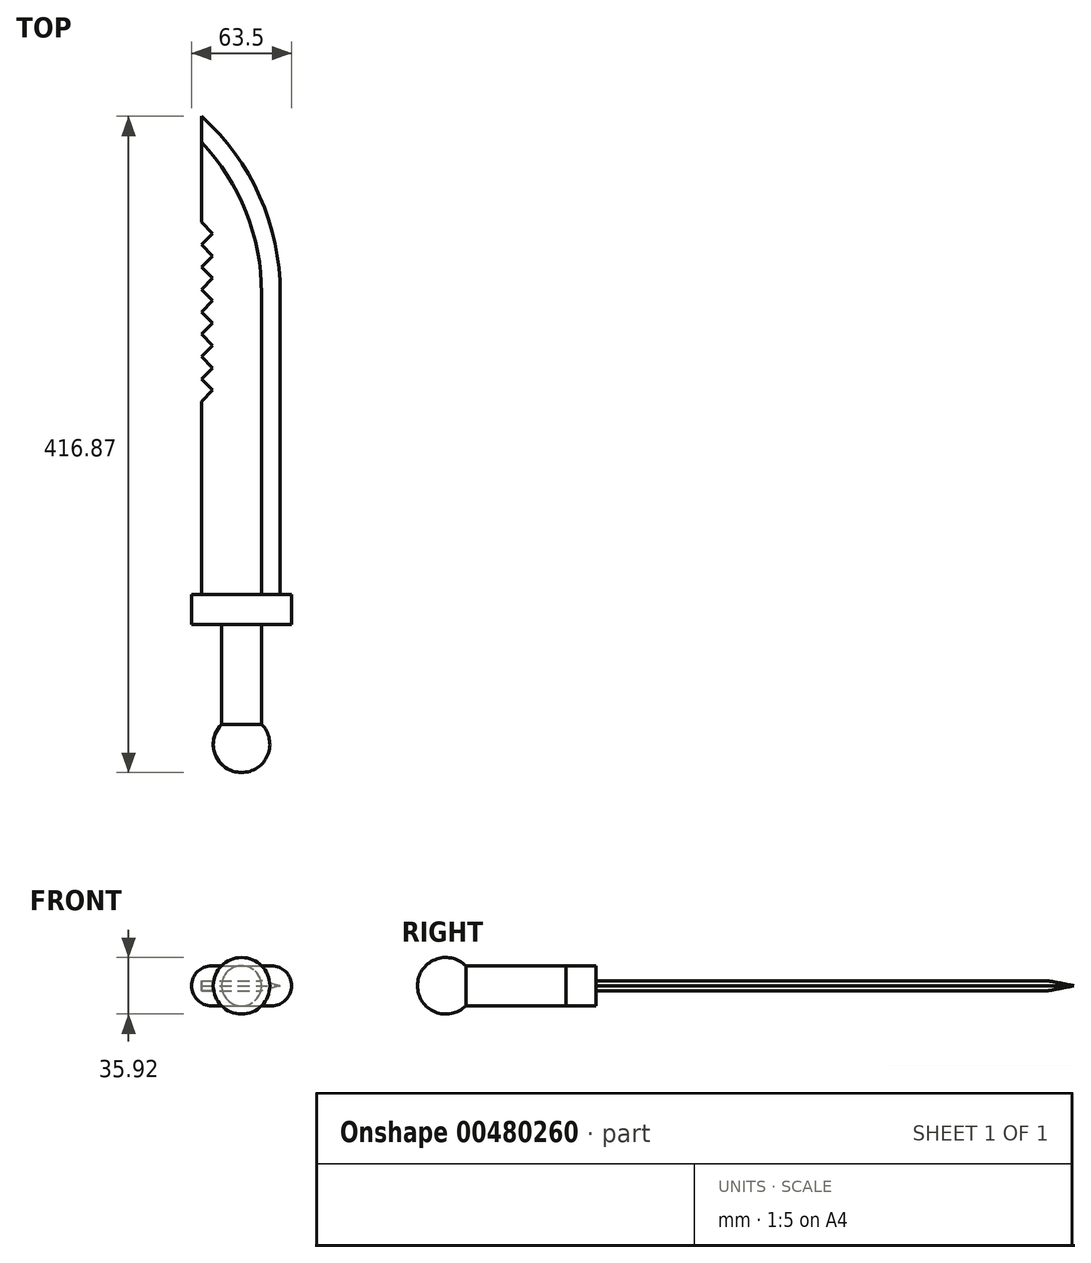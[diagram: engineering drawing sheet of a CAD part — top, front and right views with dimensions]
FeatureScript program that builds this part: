
annotation { "Feature Type Name" : "Feature", "Feature Type Description" : "" }
export const myFeature = defineFeature(function(context is Context, id is Id, definition is map)
    precondition{}
    {
        {
            var Q0;
            Q0=qCreatedBy(makeId("Front.planeOp"),FACE);
            var sketch = newSketch(context, id + "F0", { "sketchPlane" : qUnion([Q0])});
            skLineSegment(sketch, "E0", {"start": v(0, 0) * mm, "end": v(-25.4, 0) * mm});
            skLineSegment(sketch, "E1", {"start": v(-25.4, 0) * mm, "end": v(-25.4, 3.17) * mm});
            skLineSegment(sketch, "E2", {"start": v(-25.4, 3.17) * mm, "end": v(25.4, 3.17) * mm});
            skLineSegment(sketch, "E3", {"start": v(0, 0) * mm, "end": v(25.4, 0) * mm});
            skLineSegment(sketch, "E4", {"start": v(25.4, 0) * mm, "end": v(25.4, 3.18) * mm});
            skLineSegment(sketch, "E5.MirrorCS", {"start": v(-25.4, 0) * mm, "end": v(-25.4, -3.17) * mm});
            skLineSegment(sketch, "E6.MirrorCS", {"start": v(-25.4, -3.17) * mm, "end": v(25.4, -3.17) * mm});
            skLineSegment(sketch, "E7.MirrorCS", {"start": v(25.4, 0) * mm, "end": v(25.4, -3.18) * mm});
            skSolve(sketch);
        }
        {
            var Q0;
            Q0=makeQuery(id+"F0.imprint","IMPRINT",FACE,{"disambiguationData":[TD([[makeQuery(id+"F0.imprint","IMPRINT",EDGE,{"derivedFrom":sQuery(id+"F0.wireOp",EDGE,"E0")}),-1.0]])]});
            var Q1;
            Q1=makeQuery(id+"F0.imprint","IMPRINT",FACE,{"disambiguationData":[TD([[makeQuery(id+"F0.imprint","IMPRINT",EDGE,{"derivedFrom":sQuery(id+"F0.wireOp",EDGE,"E0")}),1.0]])]});
            extrude(context, id + "F1", {"entities" : qUnion([Q0, Q1]), "oppositeDirection" : true, "depth" : 304.8 * mm});
        }
        {
            var Q0;
            Q0=makeQuery(id+"F1.opExtrude","CAP_EDGE",EDGE,{"disambiguationData":[OSD([sQuery(id+"F0.wireOp",EDGE,"E4"),sQuery(id+"F0.wireOp",EDGE,"E7.MirrorCS")])],"isStart":false});
            fillet(context, id + "F2", {"entities" : qUnion([Q0]), "radius" : 152.4 * mm, "tangentPropagation" : true, "allowEdgeOverflow" : false});
        }
        {
            var Q0;
            Q0=makeQuery(id+"F2.opFillet","BLEND_EDGE",EDGE,{"blendedFrom":[makeQuery(id+"F1.opExtrude","CAP_EDGE",EDGE,{"disambiguationData":[OSD([sQuery(id+"F0.wireOp",EDGE,"E4"),sQuery(id+"F0.wireOp",EDGE,"E7.MirrorCS")])],"isStart":false}),makeQuery(id+"F1.opExtrude","SWEPT_FACE",FACE,{"disambiguationData":[OSD([sQuery(id+"F0.wireOp",EDGE,"E2")])]})],"blendedInto":[makeQuery(id+"F1.opExtrude","SWEPT_FACE",FACE,{"disambiguationData":[OSD([sQuery(id+"F0.wireOp",EDGE,"E2")])]})]});
            var Q1;
            Q1=makeQuery(id+"F1.opExtrude","SWEPT_EDGE",EDGE,{"disambiguationData":[OSD([sQuery(id+"F0.wireOp",EDGE,"E2"),sQuery(id+"F0.wireOp",EDGE,"E4")])]});
            var Q2;
            Q2=makeQuery(id+"F1.opExtrude","SWEPT_EDGE",EDGE,{"disambiguationData":[OSD([sQuery(id+"F0.wireOp",EDGE,"E6.MirrorCS"),sQuery(id+"F0.wireOp",EDGE,"E7.MirrorCS")])]});
            var Q3;
            Q3=makeQuery(id+"F2.opFillet","BLEND_EDGE",EDGE,{"blendedFrom":[makeQuery(id+"F1.opExtrude","CAP_EDGE",EDGE,{"disambiguationData":[OSD([sQuery(id+"F0.wireOp",EDGE,"E4"),sQuery(id+"F0.wireOp",EDGE,"E7.MirrorCS")])],"isStart":false}),makeQuery(id+"F1.opExtrude","SWEPT_FACE",FACE,{"disambiguationData":[OSD([sQuery(id+"F0.wireOp",EDGE,"E6.MirrorCS")])]})],"blendedInto":[makeQuery(id+"F1.opExtrude","SWEPT_FACE",FACE,{"disambiguationData":[OSD([sQuery(id+"F0.wireOp",EDGE,"E6.MirrorCS")])]})]});
            chamfer(context, id + "F3", {"entities" : qUnion([Q0, Q1, Q2, Q3]), "chamferType" : ChamferType.OFFSET_ANGLE, "width" : 12.7 * mm, "oppositeDirection" : false, "angle" : 15 * degree, "tangentPropagation" : true});
        }
        {
            var Q0;
            Q0=makeQuery(id+"F1.opExtrude","CAP_FACE",FACE,{"disambiguationData":[OSD([sQuery(id+"F0.wireOp",EDGE,"E1"),sQuery(id+"F0.wireOp",EDGE,"E2"),sQuery(id+"F0.wireOp",EDGE,"E4"),sQuery(id+"F0.wireOp",EDGE,"E5.MirrorCS"),sQuery(id+"F0.wireOp",EDGE,"E6.MirrorCS"),sQuery(id+"F0.wireOp",EDGE,"E7.MirrorCS")])],"isStart":true});
            var sketch = newSketch(context, id + "F4", { "sketchPlane" : qUnion([Q0])});
            skLineSegment(sketch, "E8", {"start": v(0, 0) * mm, "end": v(0, 12.7) * mm});
            skLineSegment(sketch, "E9", {"start": v(0, 12.7) * mm, "end": v(-31.75, 12.7) * mm});
            skLineSegment(sketch, "E10", {"start": v(-31.75, 12.7) * mm, "end": v(-31.75, -12.7) * mm});
            skLineSegment(sketch, "E11", {"start": v(-31.75, -12.7) * mm, "end": v(0, -12.7) * mm});
            skLineSegment(sketch, "E12.MirrorCS", {"start": v(0, 12.7) * mm, "end": v(31.75, 12.7) * mm});
            skLineSegment(sketch, "E13.MirrorCS", {"start": v(31.75, 12.7) * mm, "end": v(31.75, -12.7) * mm});
            skLineSegment(sketch, "E14.MirrorCS", {"start": v(31.75, -12.7) * mm, "end": v(0, -12.7) * mm});
            skSolve(sketch);
        }
        {
            var Q0;
            Q0=makeQuery(id+"F4.imprint","IMPRINT",FACE,{"disambiguationData":[TD([[makeQuery(id+"F4.imprint","IMPRINT",EDGE,{"derivedFrom":sQuery(id+"F4.wireOp",EDGE,"E9")}),1.0]])]});
            var Q1;
            {var subQ0=sQuery(id+"F0.wireOp",EDGE,"E6.MirrorCS");Q1=makeQuery(id+"F4.imprint","IMPRINT",FACE,{"disambiguationData":[TD([[makeQuery(id+"F4.imprint","IMPRINT",EDGE,{"derivedFrom":makeQuery(id+"F1.opExtrude","CAP_EDGE",EDGE,{"disambiguationData":[OSD([subQ0])],"isStart":true})}),1.0]])]});}
            extrude(context, id + "F5", {"entities" : qUnion([Q0, Q1]), "operationType" : NewBodyOperationType.ADD, "depth" : 19.05 * mm});
        }
        {
            var Q0;
            Q0=makeQuery(id+"F5.opExtrude","CAP_FACE",FACE,{"disambiguationData":[OSD([sQuery(id+"F4.wireOp",EDGE,"E9"),sQuery(id+"F4.wireOp",EDGE,"E10"),sQuery(id+"F4.wireOp",EDGE,"E11"),sQuery(id+"F4.wireOp",EDGE,"E12.MirrorCS"),sQuery(id+"F4.wireOp",EDGE,"E13.MirrorCS"),sQuery(id+"F4.wireOp",EDGE,"E14.MirrorCS")])],"isStart":false});
            var sketch = newSketch(context, id + "F6", { "sketchPlane" : qUnion([Q0])});
            skCircle(sketch, "E15", {"center": v(0, 0) * mm, "radius": 12.7 * mm});
            skSolve(sketch);
        }
        {
            var Q0;
            {var subQ0=sQuery(id+"F6.wireOp",EDGE,"E15");var subQ1=makeQuery(id+"F6.imprint","INTERSECT",VERTEX,{"derivedFrom":[makeQuery(id+"F5.opExtrude","CAP_EDGE",EDGE,{"disambiguationData":[OSD([sQuery(id+"F4.wireOp",EDGE,"E9"),sQuery(id+"F4.wireOp",EDGE,"E12.MirrorCS")])],"isStart":false}),subQ0]});Q0=makeQuery(id+"F6.imprint","IMPRINT",FACE,{"disambiguationData":[TD([[makeQuery(id+"F6.imprint","IMPRINT",EDGE,{"disambiguationData":[TD([[subQ1,-1.0]])],"derivedFrom":subQ0}),1.0]])]});}
            extrude(context, id + "F7", {"entities" : qUnion([Q0]), "operationType" : NewBodyOperationType.ADD, "depth" : 63.5 * mm});
        }
        {
            var Q0;
            Q0=makeQuery(id+"F5.opExtrude","SWEPT_EDGE",EDGE,{"disambiguationData":[OSD([sQuery(id+"F4.wireOp",EDGE,"E9"),sQuery(id+"F4.wireOp",EDGE,"E10")])]});
            var Q1;
            Q1=makeQuery(id+"F5.opExtrude","SWEPT_EDGE",EDGE,{"disambiguationData":[OSD([sQuery(id+"F4.wireOp",EDGE,"E12.MirrorCS"),sQuery(id+"F4.wireOp",EDGE,"E13.MirrorCS")])]});
            var Q2;
            Q2=makeQuery(id+"F5.opExtrude","SWEPT_EDGE",EDGE,{"disambiguationData":[OSD([sQuery(id+"F4.wireOp",EDGE,"E13.MirrorCS"),sQuery(id+"F4.wireOp",EDGE,"E14.MirrorCS")])]});
            var Q3;
            Q3=makeQuery(id+"F5.opExtrude","SWEPT_EDGE",EDGE,{"disambiguationData":[OSD([sQuery(id+"F4.wireOp",EDGE,"E10"),sQuery(id+"F4.wireOp",EDGE,"E11")])]});
            fillet(context, id + "F8", {"entities" : qUnion([Q0, Q1, Q2, Q3]), "radius" : 12.7 * mm, "tangentPropagation" : true, "allowEdgeOverflow" : false});
        }
        {
            var Q0;
            Q0=qCreatedBy(makeId("Top.planeOp"),FACE);
            var sketch = newSketch(context, id + "F9", { "sketchPlane" : qUnion([Q0])});
            skLineSegment(sketch, "E16", {"start": v(0, 0) * mm, "end": v(0, -82.55) * mm});
            skLineSegment(sketch, "E17", {"start": v(0, -82.55) * mm, "end": v(0, -113.21) * mm});
            skLineSegment(sketch, "E18", {"start": v(0, -82.55) * mm, "end": v(-12.7, -82.55) * mm});
            skCircle(sketch, "E19", {"center": v(0, -95.25) * mm, "radius": 17.96 * mm});
            skLineSegment(sketch, "E20", {"start": v(0, -82.55) * mm, "end": v(12.7, -82.55) * mm});
            skSolve(sketch);
        }
        {
            var Q0;
            {var subQ0=sQuery(id+"F9.wireOp",EDGE,"E18");Q0=makeQuery(id+"F9.imprint","IMPRINT",FACE,{"disambiguationData":[TD([[makeQuery(id+"F9.imprint","IMPRINT",EDGE,{"derivedFrom":subQ0}),1.0]])]});}
            var Q1;
            Q1=sQuery(id+"F9.wireOp",EDGE,"E17");
            revolve(context, id + "F10", {"entities" : qUnion([Q0]), "axis" : qUnion([Q1]), "revolveType" : RevolveType.ONE_DIRECTION, "oppositeDirection" : true, "angle" : 360 * degree});
        }
        {
            var Q0;
            Q0=makeQuery(id+"F1.opExtrude","SWEPT_FACE",FACE,{"disambiguationData":[OSD([sQuery(id+"F0.wireOp",EDGE,"E2")])]});
            var sketch = newSketch(context, id + "F11", { "sketchPlane" : qUnion([Q0])});
            skLineSegment(sketch, "E21", {"start": v(-25.4, 287.1) * mm, "end": v(-25.4, 236.3) * mm});
            skLineSegment(sketch, "E22", {"start": v(-25.4, 236.3) * mm, "end": v(-18.29, 229.18) * mm});
            skLineSegment(sketch, "E23", {"start": v(-25.4, 236.3) * mm, "end": v(-25.4, 222.07) * mm});
            skLineSegment(sketch, "E24", {"start": v(-25.4, 222.07) * mm, "end": v(-18.29, 229.18) * mm});
            skLineSegment(sketch, "E25", {"start": v(-25.4, 222.07) * mm, "end": v(-22.15, 222.07) * mm});
            skLineSegment(sketch, "E26.MirrorCS", {"start": v(-25.4, 207.85) * mm, "end": v(-25.4, 222.07) * mm});
            skLineSegment(sketch, "E27.MirrorCS", {"start": v(-25.4, 207.85) * mm, "end": v(-18.29, 214.96) * mm});
            skLineSegment(sketch, "E28.MirrorCS", {"start": v(-25.4, 222.07) * mm, "end": v(-18.29, 214.96) * mm});
            skLineSegment(sketch, "E29", {"start": v(-25.4, 207.85) * mm, "end": v(-20.29, 207.85) * mm});
            skLineSegment(sketch, "E30.MirrorCS", {"start": v(-25.4, 179.4) * mm, "end": v(-18.29, 186.52) * mm});
            skLineSegment(sketch, "E31.MirrorCS", {"start": v(-25.4, 179.4) * mm, "end": v(-25.4, 193.63) * mm});
            skLineSegment(sketch, "E32.MirrorCS", {"start": v(-25.4, 193.63) * mm, "end": v(-18.29, 186.52) * mm});
            skLineSegment(sketch, "E33.MirrorCS", {"start": v(-25.4, 193.63) * mm, "end": v(-18.29, 200.74) * mm});
            skLineSegment(sketch, "E34.MirrorCS", {"start": v(-25.4, 207.85) * mm, "end": v(-25.4, 193.63) * mm});
            skLineSegment(sketch, "E35.MirrorCS", {"start": v(-25.4, 207.85) * mm, "end": v(-18.29, 200.74) * mm});
            skLineSegment(sketch, "E36", {"start": v(-25.4, 179.4) * mm, "end": v(-11.9, 179.4) * mm});
            skLineSegment(sketch, "E37.MirrorCS", {"start": v(-25.4, 122.53) * mm, "end": v(-18.29, 129.64) * mm});
            skLineSegment(sketch, "E38.MirrorCS", {"start": v(-25.4, 122.53) * mm, "end": v(-25.4, 136.75) * mm});
            skLineSegment(sketch, "E39.MirrorCS", {"start": v(-25.4, 136.75) * mm, "end": v(-18.29, 129.64) * mm});
            skLineSegment(sketch, "E40.MirrorCS", {"start": v(-25.4, 136.75) * mm, "end": v(-18.29, 143.86) * mm});
            skLineSegment(sketch, "E41.MirrorCS", {"start": v(-25.4, 150.97) * mm, "end": v(-25.4, 136.75) * mm});
            skLineSegment(sketch, "E42.MirrorCS", {"start": v(-25.4, 150.97) * mm, "end": v(-18.29, 143.86) * mm});
            skLineSegment(sketch, "E43.MirrorCS", {"start": v(-25.4, 150.97) * mm, "end": v(-18.29, 158.08) * mm});
            skLineSegment(sketch, "E44.MirrorCS", {"start": v(-25.4, 150.97) * mm, "end": v(-25.4, 165.19) * mm});
            skLineSegment(sketch, "E45.MirrorCS", {"start": v(-25.4, 165.19) * mm, "end": v(-18.29, 158.08) * mm});
            skLineSegment(sketch, "E46.MirrorCS", {"start": v(-25.4, 165.19) * mm, "end": v(-18.29, 172.3) * mm});
            skLineSegment(sketch, "E47.MirrorCS", {"start": v(-25.4, 179.4) * mm, "end": v(-25.4, 165.19) * mm});
            skLineSegment(sketch, "E48.MirrorCS", {"start": v(-25.4, 179.4) * mm, "end": v(-18.29, 172.3) * mm});
            skSolve(sketch);
        }
        {
            var Q0;
            Q0=makeQuery(id+"F11.imprint","IMPRINT",FACE,{"disambiguationData":[TD([[makeQuery(id+"F11.imprint","IMPRINT",EDGE,{"derivedFrom":sQuery(id+"F11.wireOp",EDGE,"E22")}),-1.0]])]});
            var Q1;
            Q1=makeQuery(id+"F11.imprint","IMPRINT",FACE,{"disambiguationData":[TD([[makeQuery(id+"F11.imprint","IMPRINT",EDGE,{"derivedFrom":sQuery(id+"F11.wireOp",EDGE,"E26.MirrorCS")}),1.0]])]});
            var Q2;
            Q2=makeQuery(id+"F11.imprint","IMPRINT",FACE,{"disambiguationData":[TD([[makeQuery(id+"F11.imprint","IMPRINT",EDGE,{"derivedFrom":sQuery(id+"F11.wireOp",EDGE,"E33.MirrorCS")}),1.0]])]});
            var Q3;
            Q3=makeQuery(id+"F11.imprint","IMPRINT",FACE,{"disambiguationData":[TD([[makeQuery(id+"F11.imprint","IMPRINT",EDGE,{"derivedFrom":sQuery(id+"F11.wireOp",EDGE,"E30.MirrorCS")}),1.0]])]});
            var Q4;
            Q4=makeQuery(id+"F11.imprint","IMPRINT",FACE,{"disambiguationData":[TD([[makeQuery(id+"F11.imprint","IMPRINT",EDGE,{"derivedFrom":sQuery(id+"F11.wireOp",EDGE,"E46.MirrorCS")}),1.0]])]});
            var Q5;
            Q5=makeQuery(id+"F11.imprint","IMPRINT",FACE,{"disambiguationData":[TD([[makeQuery(id+"F11.imprint","IMPRINT",EDGE,{"derivedFrom":sQuery(id+"F11.wireOp",EDGE,"E43.MirrorCS")}),1.0]])]});
            var Q6;
            Q6=makeQuery(id+"F11.imprint","IMPRINT",FACE,{"disambiguationData":[TD([[makeQuery(id+"F11.imprint","IMPRINT",EDGE,{"derivedFrom":sQuery(id+"F11.wireOp",EDGE,"E40.MirrorCS")}),1.0]])]});
            var Q7;
            Q7=makeQuery(id+"F11.imprint","IMPRINT",FACE,{"disambiguationData":[TD([[makeQuery(id+"F11.imprint","IMPRINT",EDGE,{"derivedFrom":sQuery(id+"F11.wireOp",EDGE,"E37.MirrorCS")}),1.0]])]});
            extrude(context, id + "F12", {"entities" : qUnion([Q0, Q1, Q2, Q3, Q4, Q5, Q6, Q7]), "operationType" : NewBodyOperationType.REMOVE, "oppositeDirection" : true, "depth" : 25.4 * mm});
        }
    });
